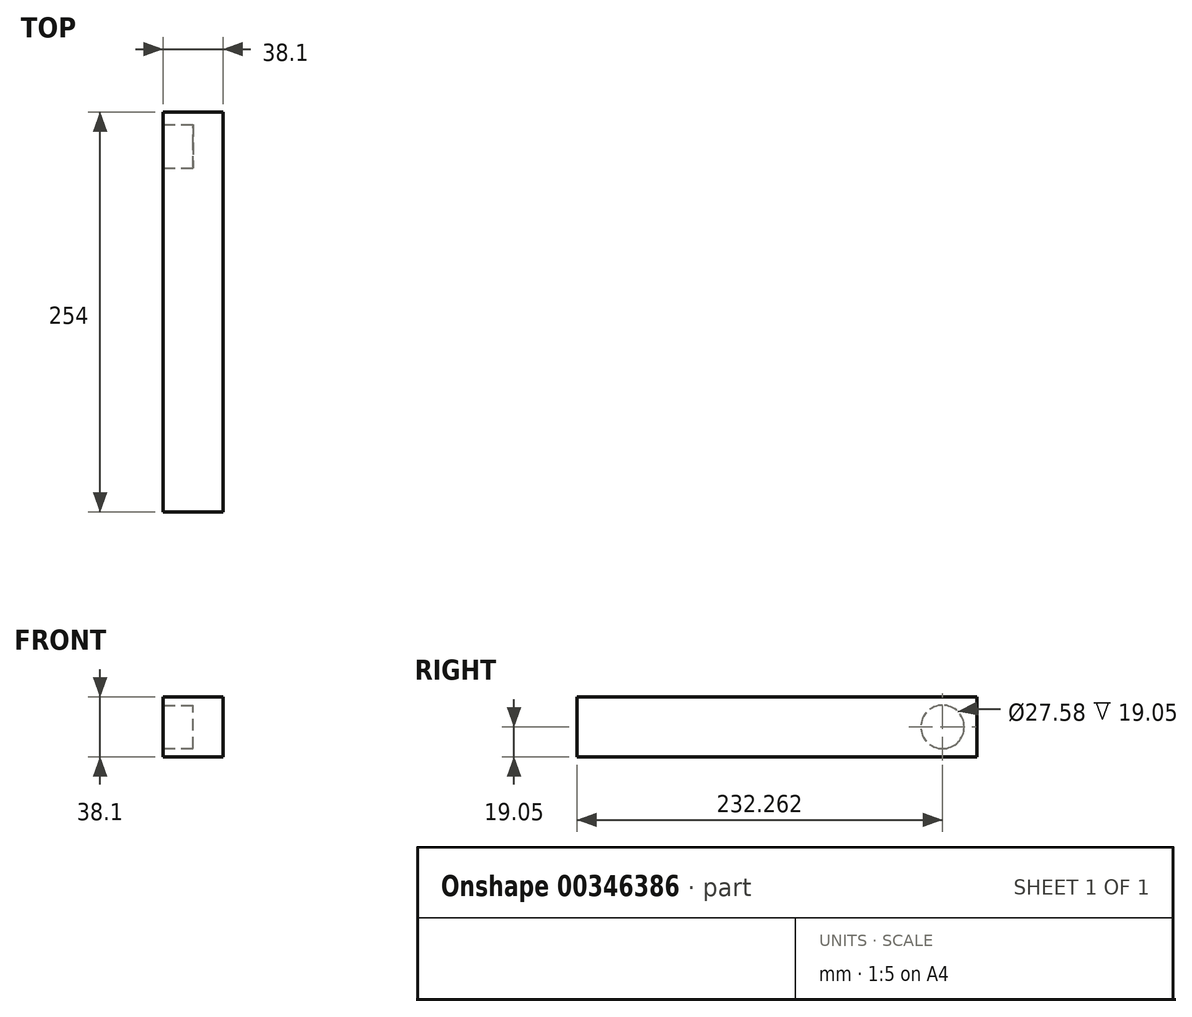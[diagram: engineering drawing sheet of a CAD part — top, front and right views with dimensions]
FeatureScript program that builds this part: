
annotation { "Feature Type Name" : "Feature", "Feature Type Description" : "" }
export const myFeature = defineFeature(function(context is Context, id is Id, definition is map)
    precondition{}
    {
        {
            var Q0;
            Q0=qCreatedBy(makeId("Front.planeOp"),FACE);
            var sketch = newSketch(context, id + "F0", { "sketchPlane" : qUnion([Q0])});
            skLineSegment(sketch, "E0.bottom", {"start": v(19.05, -19.05) * mm, "end": v(-19.05, -19.05) * mm});
            skLineSegment(sketch, "E0.top", {"start": v(19.05, 19.05) * mm, "end": v(-19.05, 19.05) * mm});
            skLineSegment(sketch, "E0.left", {"start": v(19.05, -19.05) * mm, "end": v(19.05, 19.05) * mm});
            skLineSegment(sketch, "E0.right", {"start": v(-19.05, -19.05) * mm, "end": v(-19.05, 19.05) * mm});
            skPoint(sketch, "E0.middle", {"position": v(0, 0) * mm});
            skSolve(sketch);
        }
        {
            var Q0;
            Q0 = qSketchRegion(id + "F0", true);
            extrude(context, id + "F1", {"entities" : qUnion([Q0]), "depth" : 254 * mm});
        }
        {
            var Q0;
            Q0=qCreatedBy(makeId("Right.planeOp"),FACE);
            var sketch = newSketch(context, id + "F2", { "sketchPlane" : qUnion([Q0])});
            skCircle(sketch, "E1", {"center": v(-21.74, 0) * mm, "radius": 13.79 * mm});
            skSolve(sketch);
        }
        {
            var Q0;
            Q0 = qSketchRegion(id + "F2", true);
            extrude(context, id + "F3", {"entities" : qUnion([Q0]), "operationType" : NewBodyOperationType.REMOVE, "endBound" : BoundingType.THROUGH_ALL, "oppositeDirection" : true, "depth" : 25.4 * mm});
        }
    });
